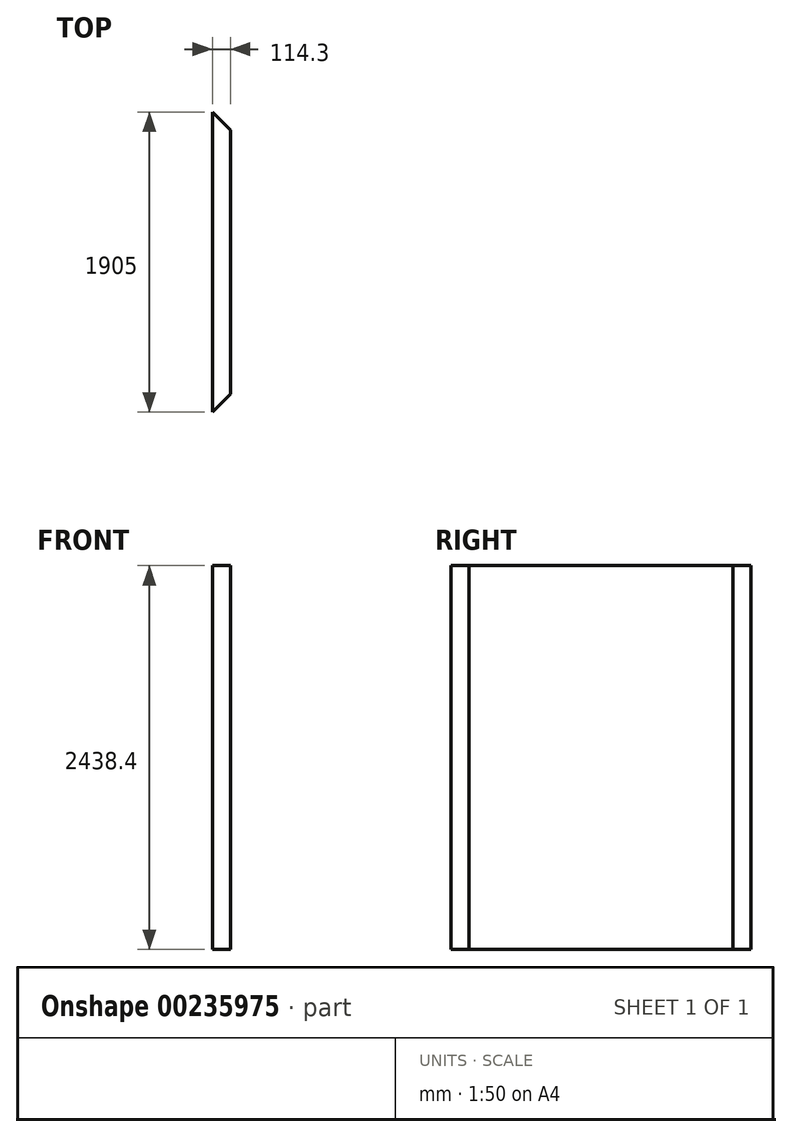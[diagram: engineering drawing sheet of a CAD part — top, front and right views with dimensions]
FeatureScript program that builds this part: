
annotation { "Feature Type Name" : "Feature", "Feature Type Description" : "" }
export const myFeature = defineFeature(function(context is Context, id is Id, definition is map)
    precondition{}
    {
        {
            var Q0;
            Q0=qCreatedBy(makeId("Top.planeOp"),FACE);
            var sketch = newSketch(context, id + "F0", { "sketchPlane" : qUnion([Q0])});
            skLineSegment(sketch, "E0.bottom", {"start": v(57.15, -838.2) * mm, "end": v(-57.15, -838.2) * mm});
            skLineSegment(sketch, "E0.top", {"start": v(57.15, 838.2) * mm, "end": v(-57.15, 838.2) * mm});
            skLineSegment(sketch, "E0.left", {"start": v(57.15, -838.2) * mm, "end": v(57.15, 838.2) * mm});
            skLineSegment(sketch, "E0.right", {"start": v(-57.15, -838.2) * mm, "end": v(-57.15, 838.2) * mm});
            skPoint(sketch, "E0.middle", {"position": v(0, 0) * mm});
            skLineSegment(sketch, "E1", {"start": v(-57.15, 838.2) * mm, "end": v(-57.15, 952.5) * mm});
            skLineSegment(sketch, "E2", {"start": v(-57.15, 952.5) * mm, "end": v(57.15, 838.2) * mm});
            skLineSegment(sketch, "E3", {"start": v(-57.15, -838.2) * mm, "end": v(-57.15, -952.5) * mm});
            skLineSegment(sketch, "E4", {"start": v(57.15, -838.2) * mm, "end": v(-57.15, -952.5) * mm});
            skSolve(sketch);
        }
        {
            var Q0;
            Q0 = qSketchRegion(id + "F0", true);
            extrude(context, id + "F1", {"entities" : qUnion([Q0]), "depth" : 2438.4 * mm});
        }
    });
